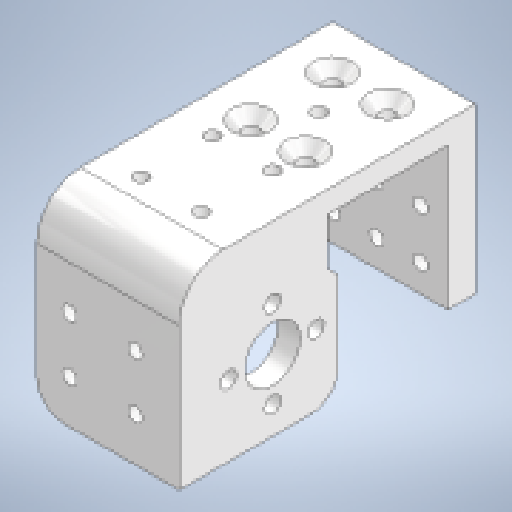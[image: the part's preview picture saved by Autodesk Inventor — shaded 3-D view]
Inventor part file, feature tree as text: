
AUTODESK INVENTOR PART (.ipt)
format: ipt  version: 2024.1 (Build 281209000, 209)  size: 432,640 bytes
history: native  units: mm
features: extrude x12, sketch x12, fillet x3, chamfer x2
ambient origin geometry x8: Origin, YZ Plane, XZ Plane, XY Plane, X Axis, Y Axis, Z Axis, Center Point
bodies: Solid1 (feature_tree)
feature tree (29):
  extrude  "Extrusion1"  Depth=26.0mm
  extrude  "Extrusion2"  Depth=4.0mm
  extrude  "Extrusion3"  Depth=30.0mm TaperAngle=0.0deg
  extrude  "Extrusion4"  Depth=10.0mm
  extrude  "Extrusion6"  TaperAngle=0.0deg  [1 undecoded]
  fillet  "Fillet3"  Radius=3.0mm
  fillet  "Fillet4"  Radius=3.0mm
  fillet  "Fillet5"  Radius=3.0mm
  extrude  "Extrusion7"  Depth=8.0mm
  extrude  "Extrusion8"  Depth=8.0mm
  extrude  "Extrusion9"  Depth=8.0mm
  chamfer  "Chamfer3"  [1 undecoded]
  extrude  "Extrusion10"  Depth=5.0mm
  extrude  "Extrusion11"  Depth=1.5mm
  extrude  "Extrusion13"  Depth=30.0mm
  chamfer  "Chamfer4"  Distance=5.0mm
  extrude  "Extrusion14"  Depth=2.0mm
  sketch  "Sketch1"  dims[d0=45.0mm d1=26.0mm]
  sketch  "Sketch2"  dims[d2=4.0mm d3=0.0mm d4=4.0mm]
  sketch  "Sketch4"  dims[d5=25.0mm d6=30.0mm d7=0.0mm]
  sketch  "Sketch5"  dims[d8=10.0mm d9=13.0mm]
  sketch  "Sketch9"  dims[d10=13.0mm d11=0.0mm d12=0.0mm d13=3.0mm d14=3.0mm d15=3.0mm]
  sketch  "Sketch10"  dims[d16=3.0mm d17=8.0mm]
  sketch  "Sketch12"  dims[d19=8.0mm d20=8.0mm]
  sketch  "Sketch13"  dims[d21=8.0mm d22=8.0mm]
  sketch  "Sketch14"  dims[d23=8.0mm]
  sketch  "Sketch15"  dims[d24=8.0mm d25=0.0mm d26=0.0mm]
  sketch  "Sketch18"  dims[d39=4.0mm d40=0.0mm d41=5.0mm]
  sketch  "Sketch19"  dims[d42=8.0mm d43=1.5mm d44=30.0mm d45=5.0mm d46=0.0mm d47=2.6mm d48=2.6mm d49=2.6mm d50=2.6mm d51=2.6mm d52=5.0mm d53=5.0mm d54=5.0mm d55=5.0mm d56=7.0mm d57=7.0mm d58=16.0mm d59=5.0mm d60=5.0mm d61=5.0mm d62=10.0mm d63=0.0mm d64=2.6mm d65=16.0mm d66=5.0mm d67=3.0mm d68=3.0mm d69=3.0mm d70=3.0mm d71=10.0mm d72=15.0mm d73=15.0mm d74=8.0mm d75=8.0mm d76=8.0mm d77=8.0mm d78=10.0mm d79=0.0mm d80=0.0mm d81=2.6mm d82=2.6mm d83=2.6mm d84=5.0mm d85=13.0mm d86=13.0mm d87=13.0mm d88=7.0mm d89=16.0mm d90=2.0mm d91=2.0mm d92=45.0deg d93=2.6mm d94=2.6mm d95=2.6mm d96=2.6mm d97=8.0mm d98=8.0mm d99=6.0mm d100=6.0mm d101=8.0mm d102=8.0mm d103=10.0mm d104=10.0mm d105=0.0mm d106=0.0mm d107=2.6mm d108=2.6mm d109=2.6mm d110=2.6mm d111=8.0mm d112=8.0mm d113=7.0mm d114=7.0mm d115=13.0mm d116=13.0mm d117=29.0mm d118=29.0mm d119=10.0mm d120=0.0mm d124=8.5mm d125=2.0mm d126=0.0mm d127=0.0mm d128=2.0mm d129=2.0mm d130=45.0deg d131=2.6mm d132=15.5mm d133=13.0mm d134=0.0mm d135=0.0mm]
note: 2 required parameter values undecoded (feature->parameter linkage not recoverable at this tier; creation-order binding heuristic only, values carry confidence <= 0.55)
